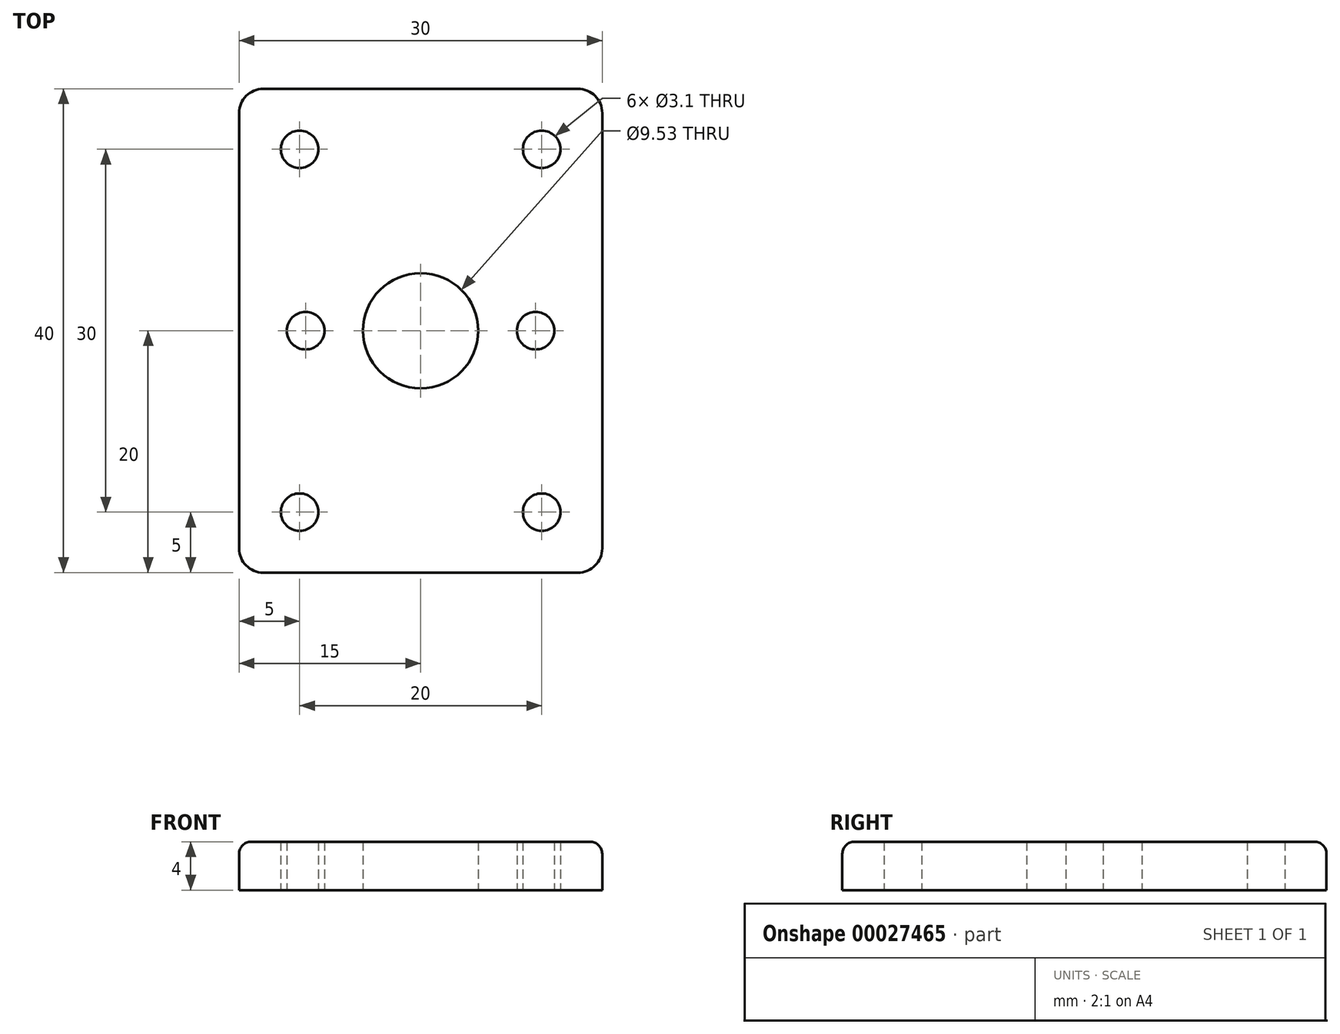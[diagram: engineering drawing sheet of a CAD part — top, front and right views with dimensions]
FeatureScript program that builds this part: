
annotation { "Feature Type Name" : "Feature", "Feature Type Description" : "" }
export const myFeature = defineFeature(function(context is Context, id is Id, definition is map)
    precondition{}
    {
        {
            var Q0;
            Q0=qCreatedBy(makeId("Top.planeOp"),FACE);
            var sketch = newSketch(context, id + "F0", { "sketchPlane" : qUnion([Q0])});
            skLineSegment(sketch, "E0.rect.bottom", {"start": v(13, -20) * mm, "end": v(-13, -20) * mm});
            skLineSegment(sketch, "E0.rect.top", {"start": v(13, 20) * mm, "end": v(-13, 20) * mm});
            skLineSegment(sketch, "E0.rect.left", {"start": v(15, -18) * mm, "end": v(15, 18) * mm});
            skLineSegment(sketch, "E0.rect.right", {"start": v(-15, -18) * mm, "end": v(-15, 18) * mm});
            skPoint(sketch, "E0.rect.middle", {"position": v(0, 0) * mm});
            skCircle(sketch, "E1", {"center": v(0, 0) * mm, "radius": 4.76 * mm});
            skCircle(sketch, "E2", {"center": v(-10, -15) * mm, "radius": 1.55 * mm});
            skCircle(sketch, "E3.1.0.0", {"center": v(10, -15) * mm, "radius": 1.55 * mm});
            skLineSegment(sketch, "E3.direction1", {"start": v(-10, -15) * mm, "end": v(10, -15) * mm, "construction": true});
            skCircle(sketch, "E4.1.0", {"center": v(-10, 15) * mm, "radius": 1.55 * mm});
            skCircle(sketch, "E4.1.1", {"center": v(10, 15) * mm, "radius": 1.55 * mm});
            skCircle(sketch, "E5", {"center": v(9.5, 0) * mm, "radius": 1.55 * mm});
            skCircle(sketch, "E6", {"center": v(-9.5, 0) * mm, "radius": 1.55 * mm});
            skPoint(sketch, "E7.visualSharp", {"position": v(-15, -20) * mm});
            skArc(sketch, "E7.filletArc", {"start": v(-15, -18) * mm, "mid": v(-14.41, -19.41) * mm, "end": v(-13, -20) * mm});
            skPoint(sketch, "E8.visualSharp", {"position": v(-15, 20) * mm});
            skArc(sketch, "E8.filletArc", {"start": v(-13, 20) * mm, "mid": v(-14.41, 19.41) * mm, "end": v(-15, 18) * mm});
            skPoint(sketch, "E9.visualSharp", {"position": v(15, 20) * mm});
            skArc(sketch, "E9.filletArc", {"start": v(15, 18) * mm, "mid": v(14.41, 19.41) * mm, "end": v(13, 20) * mm});
            skPoint(sketch, "E10.visualSharp", {"position": v(15, -20) * mm});
            skArc(sketch, "E10.filletArc", {"start": v(13, -20) * mm, "mid": v(14.41, -19.41) * mm, "end": v(15, -18) * mm});
            skSolve(sketch);
        }
        {
            var Q0;
            Q0=makeQuery(id+"F0.imprint","IMPRINT",FACE,{"disambiguationData":[TD([[makeQuery(id+"F0.imprint","IMPRINT",EDGE,{"derivedFrom":sQuery(id+"F0.wireOp",EDGE,"E0.rect.bottom")}),-1.0]])]});
            extrude(context, id + "F1", {"entities" : qUnion([Q0]), "depth" : 4 * mm});
        }
        {
            var Q0;
            Q0=makeQuery(id+"F1.opExtrude","CAP_EDGE",EDGE,{"disambiguationData":[OSD([sQuery(id+"F0.wireOp",EDGE,"E0.rect.bottom")])],"isStart":false});
            var Q1;
            Q1=makeQuery(id+"F1.opExtrude","CAP_EDGE",EDGE,{"disambiguationData":[OSD([sQuery(id+"F0.wireOp",EDGE,"E0.rect.right")])],"isStart":false});
            var Q2;
            Q2=makeQuery(id+"F1.opExtrude","CAP_EDGE",EDGE,{"disambiguationData":[OSD([sQuery(id+"F0.wireOp",EDGE,"E7.filletArc")])],"isStart":false});
            var Q3;
            Q3=makeQuery(id+"F1.opExtrude","CAP_EDGE",EDGE,{"disambiguationData":[OSD([sQuery(id+"F0.wireOp",EDGE,"E0.rect.left")])],"isStart":false});
            var Q4;
            Q4=makeQuery(id+"F1.opExtrude","CAP_EDGE",EDGE,{"disambiguationData":[OSD([sQuery(id+"F0.wireOp",EDGE,"E10.filletArc")])],"isStart":false});
            var Q5;
            Q5=makeQuery(id+"F1.opExtrude","CAP_EDGE",EDGE,{"disambiguationData":[OSD([sQuery(id+"F0.wireOp",EDGE,"E0.rect.top")])],"isStart":false});
            var Q6;
            Q6=makeQuery(id+"F1.opExtrude","CAP_EDGE",EDGE,{"disambiguationData":[OSD([sQuery(id+"F0.wireOp",EDGE,"E8.filletArc")])],"isStart":false});
            var Q7;
            Q7=makeQuery(id+"F1.opExtrude","CAP_EDGE",EDGE,{"disambiguationData":[OSD([sQuery(id+"F0.wireOp",EDGE,"E9.filletArc")])],"isStart":false});
            fillet(context, id + "F2", {"entities" : qUnion([Q0, Q1, Q2, Q3, Q4, Q5, Q6, Q7]), "radius" : 1 * mm, "tangentPropagation" : true, "allowEdgeOverflow" : false});
        }
    });
